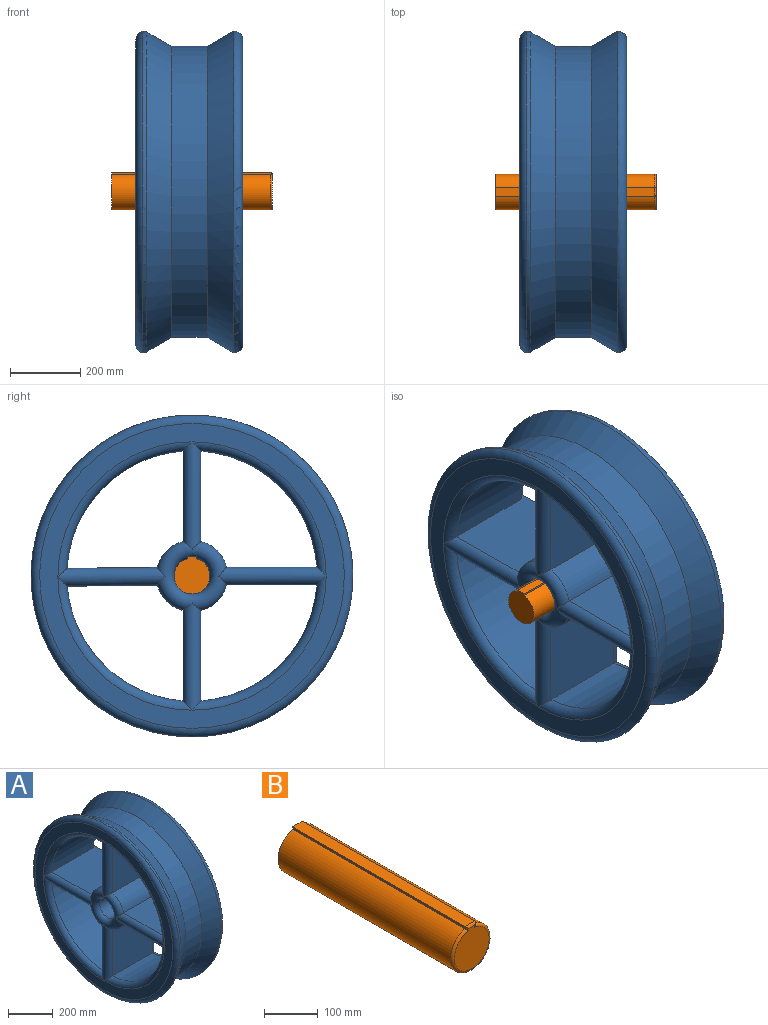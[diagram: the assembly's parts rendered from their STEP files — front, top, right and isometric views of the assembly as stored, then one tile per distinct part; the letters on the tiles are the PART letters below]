
ASSEMBLY  parts=2 mates=1
PART A: 46 faces, bbox 303.7x991.8x991.8 mm
  f0: plane 865.46x865.46mm, normal (-1,0,0), area 132239.7mm2, adj f25,f28,f31,f32,f44
  f1: plane 863.6x863.6mm, normal (1,0,0), area 137488.3mm2, adj f16,f35,f36,f38,f39,f41,f43,f45
  f2: cone r=413.51mm half-angle=30deg, axis (1,0,0), area 239006.5mm2, adj f3,f45
  f3: cylinder r=413.51mm len=827.03mm, axis (-1,0,0), area 263974.8mm2, adj f2,f4
  f4: cone r=457.2mm half-angle=30deg, axis (-1,0,0), area 219528.1mm2, adj f3,f34
  f5: cylinder r=50.8mm len=252.94mm, axis (1,0,0), area 74240.5mm2, adj f6,f8,f29,f41
  f6: plane 283.03x5.09mm, normal (0,-1,0), area 1388.9mm2, adj f5,f7,f29,f41
  f7: plane 283.04x25.41mm, normal (0,0,-1), area 7115.1mm2, adj f6,f8,f29,f41
  f8: plane 283.03x5.09mm, normal (0,1,0), area 1388.9mm2, adj f5,f7,f29,f41
  f9: cylinder r=101.6mm len=252.94mm, axis (-1,0,0), area 27380mm2, adj f10,f12,f29,f41
  f10: plane 256.32x252.94mm, normal (0,0,1), area 64832.3mm2, adj f9,f11,f30,f40
  f11: cylinder r=355.6mm len=329.29mm, axis (-1,0,0), area 128424.3mm2, adj f10,f12,f28,f36
  f12: plane 256.32x252.94mm, normal (0,-1,0), area 64832.3mm2, adj f9,f11,f27,f37
  f13: cylinder r=101.6mm len=252.94mm, axis (-1,0,0), area 27637.6mm2, adj f14,f16,f29,f41
  f14: plane 256.32x252.94mm, normal (0,1,0), area 64832.3mm2, adj f13,f15,f27,f37
  f15: cylinder r=355.6mm len=332.85mm, axis (-1,0,0), area 129326mm2, adj f14,f16,f25,f35
  f16: plane 308.3x278.34mm, normal (0,0.01,1), area 71625mm2, adj f1,f13,f15,f26,f35,f41
  f17: cylinder r=355.6mm len=329.02mm, axis (-1,0,0), area 127522.5mm2, adj f18,f20,f31,f39
  f18: plane 256.32x252.94mm, normal (0,1,0), area 64832.3mm2, adj f17,f19,f33,f42
  f19: cylinder r=101.6mm len=252.94mm, axis (-1,0,0), area 27122.4mm2, adj f18,f20,f29,f41
  f20: plane 256.31x252.94mm, normal (0,-0.01,-1), area 64832.3mm2, adj f17,f19,f26,f38
  f21: cylinder r=101.6mm len=252.94mm, axis (-1,0,0), area 27380mm2, adj f22,f24,f29,f41
  f22: plane 256.32x252.94mm, normal (0,-1,0), area 64832.3mm2, adj f21,f23,f33,f42
  f23: cylinder r=355.6mm len=329.29mm, axis (-1,0,0), area 128424.3mm2, adj f22,f24,f32,f43
  f24: plane 256.32x252.94mm, normal (0,0,-1), area 64832.3mm2, adj f21,f23,f30,f40
  f25: torus R=381mm, axis (1,0,0), area 21719.4mm2, adj f0,f15,f26,f27
  f26: cylinder r=25.4mm len=305.29mm, axis (0,-1,0.01), area 21839.1mm2, adj f16,f20,f25,f29,f31
  f27: cylinder r=25.4mm len=304.8mm, axis (0,0,1), area 21839.1mm2, adj f12,f14,f25,f28,f29
  f28: torus R=381mm, axis (1,0,0), area 21573.5mm2, adj f0,f11,f27,f30
  f29: torus R=76.2mm, axis (1,0,0), area 32636mm2, adj f5,f6,f7,f8,f9,f13,f19,f21
  f30: cylinder r=25.4mm len=304.8mm, axis (0,-1,0), area 21839.1mm2, adj f10,f24,f28,f29,f32
  f31: torus R=381mm, axis (1,0,0), area 21427.5mm2, adj f0,f17,f26,f33
  f32: torus R=381mm, axis (1,0,0), area 21573.5mm2, adj f0,f23,f30,f33
  f33: cylinder r=25.4mm len=304.8mm, axis (0,0,1), area 21839.1mm2, adj f18,f22,f29,f31,f32
  f34: torus R=431.8mm, axis (1,0,0), area 38109.2mm2, adj f4,f44
  f35: torus R=381mm, axis (1,0,0), area 21350.7mm2, adj f1,f15,f16,f37
  f36: torus R=381mm, axis (1,0,0), area 21573.5mm2, adj f1,f11,f37,f40
  f37: cylinder r=25.4mm len=304.8mm, axis (0,0,-1), area 21839.1mm2, adj f12,f14,f35,f36,f41
  f38: cylinder r=25.4mm len=305.04mm, axis (0,1,-0.01), area 10919.5mm2, adj f1,f20,f39,f41
  f39: torus R=381mm, axis (1,0,0), area 21427.5mm2, adj f1,f17,f38,f42
  f40: cylinder r=25.4mm len=304.8mm, axis (0,-1,0), area 21839.1mm2, adj f10,f24,f36,f41,f43
  f41: torus R=76.2mm, axis (1,0,0), area 32259.5mm2, adj f1,f5,f6,f7,f8,f9,f13,f16
  f42: cylinder r=25.4mm len=304.8mm, axis (0,0,1), area 21839.1mm2, adj f18,f22,f39,f41,f43
  f43: torus R=381mm, axis (1,0,0), area 21573.5mm2, adj f1,f23,f40,f42
  f44: torus R=432.73mm, axis (-1,0,0), area 92713.8mm2, adj f0,f34
  f45: torus R=431.8mm, axis (1,0,0), area 112300.7mm2, adj f1,f2
PART B: 10 faces, bbox 110x457.2x109.3 mm
  f0: cylinder r=50.8mm len=452.12mm, axis (0,1,0), area 132703.3mm2, adj f1,f3,f5,f6
  f1: plane 452.12x5.08mm, normal (1,0,0), area 2296.8mm2, adj f0,f2,f5,f7
  f2: plane 452.12x25.4mm, normal (0,0,1), area 11483.8mm2, adj f1,f3,f5,f9
  f3: plane 452.12x5.08mm, normal (-1,0,0), area 2296.8mm2, adj f0,f2,f5,f8
  f4: plane 94.91x91.44mm, normal (0,-1,0), area 6623mm2, adj f6,f7,f8,f9
  f5: plane 105.07x101.6mm, normal (0,1,0), area 8208.9mm2, adj f0,f1,f2,f3
  f6: torus R=45.72mm, axis (0,-1,0), area 2279.7mm2, adj f0,f4,f7,f8
  f7: cylinder r=5.08mm len=9.19mm, axis (0,0,-1), area 37.5mm2, adj f1,f4,f6,f9
  f8: cylinder r=5.08mm len=9.19mm, axis (0,0,1), area 37.5mm2, adj f3,f4,f6,f9
  f9: cylinder r=5.08mm len=25.4mm, axis (1,0,0), area 173.2mm2, adj f2,f4,f7,f8
PLACE A t=(-614.98,-479.57,42.83)mm
PLACE B rot(axis=(0,0,1),90deg) t=(-836.02,-479.57,-185.75)mm
MATE parallel B.f1 <-> A.f6  axis (0,1,0) through (-609.96,-466.87,-134.03)mm
